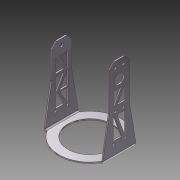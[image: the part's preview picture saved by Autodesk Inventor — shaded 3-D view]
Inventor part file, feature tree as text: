
AUTODESK INVENTOR PART (.ipt)
format: ipt  version: 2016 SP1 (Build 200210100, 210)  size: 638,464 bytes
history: native  units: in
note: dims shown in document units (in); Inventor stores cm internally (conversion verified against a paired STEP export)
features: sketch x17, other x14, extrude x4, sheet_metal_op x4, projected_geometry x3, fillet x2, plane x2, reference x2, mirror x1
ambient origin geometry x8: Origin, YZ Plane, XZ Plane, XY Plane, X Axis, Y Axis, Z Axis, Center Point
bodies: Solid1 (feature_tree)
feature tree (49):
  extrude  "Extrusion1"  Depth=2.2in
  extrude  "Extrusion2"  Depth=0.0625in
  sheet_metal_op  "Bend1"
  sheet_metal_op  "Bend2"
  fillet  "Fillet1"  Radius=0.116in
  sketch  "Sketch12"  dims[d21=0.0625in]
  extrude  "Extrusion3"  Depth=0.0625in
  sheet_metal_op  "Bend3"
  extrude  "Extrusion4"  Depth=2.808in
  sheet_metal_op  "Bend4"
  fillet  "Fillet2"  Radius=0.0625in
  plane  "Work Plane1"
  mirror  "Mirror1"
  plane  "Work Plane2"
  sketch  "Sketch1"  dims[d0=3.1in d1=2.2in]
  sketch  "Sketch2"  dims[d2=0.0625in d3=0.0in d4=2.4in d5=0.116in]
  sketch  "Sketch3"  dims[d6=2.3622in d8=360.0deg d10=0.0625in]
  sketch  "Sketch4"  dims[d11=0.0in d12=2.808in d13=0.0625in]
  sketch  "Sketch5"  dims[d14=0.0in]
  sketch  "Sketch6"  dims[d15=1.0in]
  sketch  "Sketch7"  dims[d16=1.0in]
  sketch  "Sketch8"  dims[d17=0.0625in]
  sketch  "Sketch9"  dims[d18=0.0625in]
  reference  "Reference1"
  sketch  "Sketch10"  dims[d19=4.0875in d20=0.0in]
  sketch  "Sketch13"  dims[d22=0.0312in]
  projected_geometry  "Projected Loop1"
  projected_geometry  "Projected Loop2"
  sketch  "Sketch14"  dims[d23=0.125in]
  projected_geometry  "Projected Loop3"
  reference  "Reference2"
  sketch  "Sketch19"  dims[d24=0.0625in]
  sketch  "Sketch21"  dims[d25=0.0625in]
  sketch  "Sketch22"  dims[d26=0.0625in]
  sketch  "Sketch23"  dims[d27=0.0312in d28=0.125in d29=0.0625in d30=0.0625in d31=0.0625in d32=0.0in d33=0.0312in d34=3.305in d35=0.51in d36=0.0625in d37=0.0in d38=1.8819in d39=0.4016in d40=0.5829in d41=0.1181in d42=0.0625in d43=0.0in d44=0.617in d45=0.6in d46=0.1181in d47=0.0625in d48=0.0in d49=0.0625in d50=0.0in d51=0.3in d52=0.25in d53=0.25in d54=0.25in d55=0.25in d56=0.25in d57=0.25in d58=0.25in d59=0.25in d60=0.0625in d61=0.0in d62=0.1875in d63=0.1875in d88=0.0312in d93=0.0625in d94=0.0in d95=0.0625in d96=0.0in d97=0.125in d98=0.0625in d99=0.0625in d100=0.0625in d101=0.0in d102=0.0625in d103=0.0in d104=0.125in d105=0.0625in d106=0.0625in d107=0.125in d132=0.5079in d133=0.1695in d134=0.0625in d135=0.0in d139=2.906in d142=0.312in d144=0.031in d145=0.031in d146=2.22in d148=0.062in d150=0.312in d151=0.066in d152=0.0625in d153=0.0in d154=-0.0625in d155=-0.05in d160=0.031in d161=0.031in d162=0.72in d163=1.358in d164=0.0625in d165=0.0in d166=2.9063in d167=2.22in d168=0.312in d169=0.312in d170=0.0662in d171=0.0625in d172=0.0in d173=0.031in d174=1.81in d175=0.748in d177=0.031in d178=0.082in d179=0.031in d180=0.0625in d181=0.0in]
  other  "Cut1"
  other  "Cut2"
  other  "Cut3"
  other  "Cut4"
  other  "Cut5"
  other  "Cut6"
  other  "Cut7"
  other  "Cut8"
  other  "Cut13"
  other  "Cut14"
  other  "Cut15"
  other  "Cut16"
  other  "Cut17"
  other  "Definition1"
